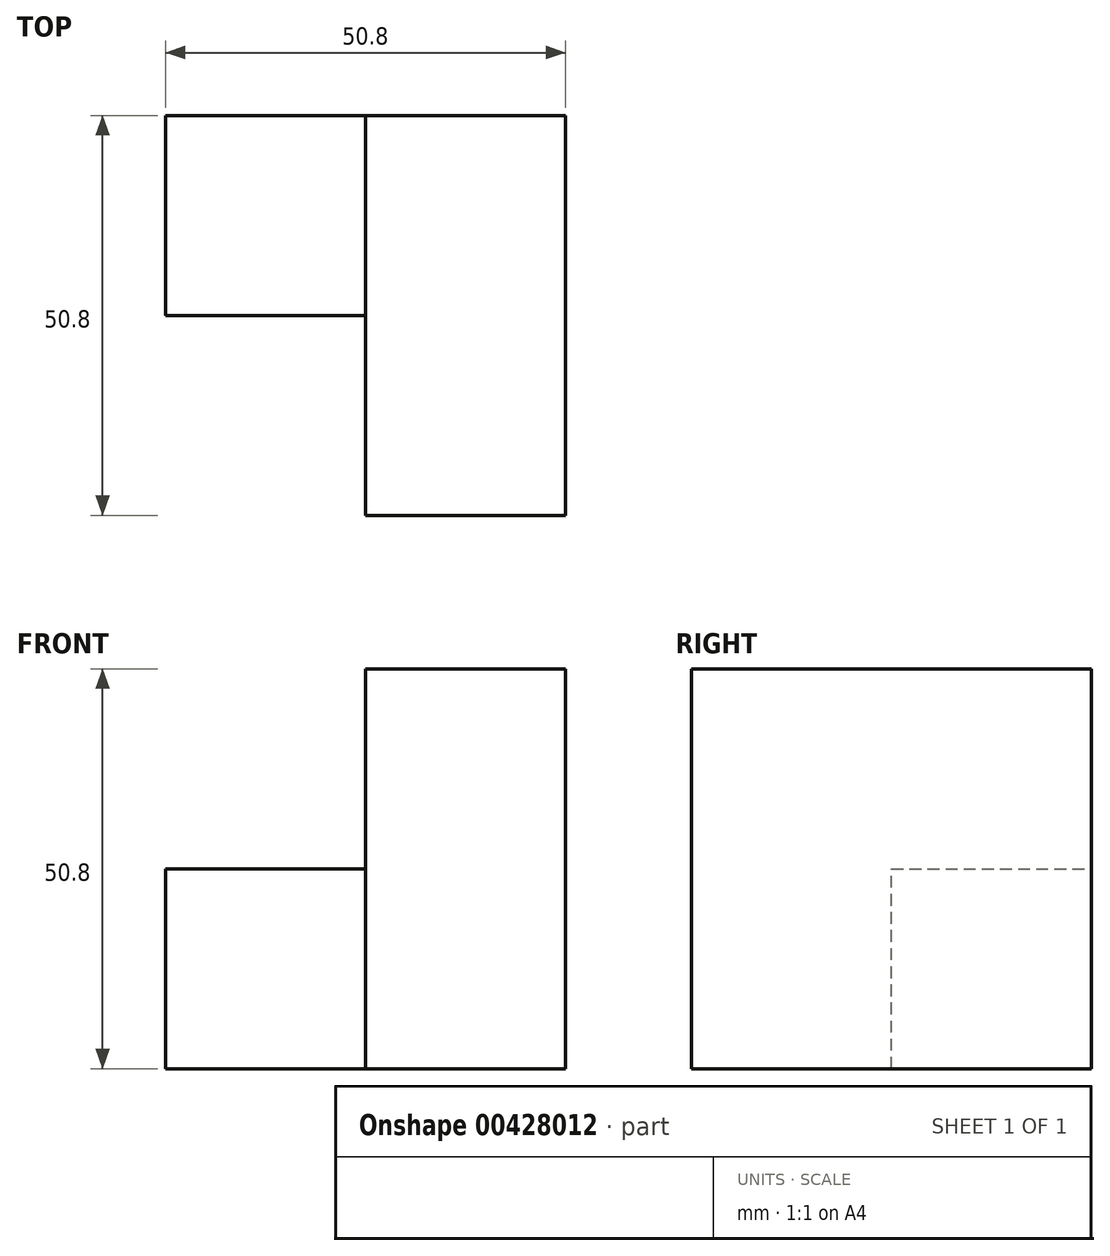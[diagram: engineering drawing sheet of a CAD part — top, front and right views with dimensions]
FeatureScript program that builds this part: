
annotation { "Feature Type Name" : "Feature", "Feature Type Description" : "" }
export const myFeature = defineFeature(function(context is Context, id is Id, definition is map)
    precondition{}
    {
        {
            var Q0;
            Q0=qCreatedBy(makeId("Front.planeOp"),FACE);
            var sketch = newSketch(context, id + "F0", { "sketchPlane" : qUnion([Q0])});
            skLineSegment(sketch, "E0.bottom", {"start": v(0, 0) * mm, "end": v(-25.4, 0) * mm});
            skLineSegment(sketch, "E0.top", {"start": v(0, 50.8) * mm, "end": v(-25.4, 50.8) * mm});
            skLineSegment(sketch, "E0.left", {"start": v(0, 0) * mm, "end": v(0, 50.8) * mm});
            skLineSegment(sketch, "E0.right", {"start": v(-25.4, 0) * mm, "end": v(-25.4, 50.8) * mm});
            skSolve(sketch);
        }
        {
            var Q0;
            Q0 = qSketchRegion(id + "F0", true);
            extrude(context, id + "F1", {"entities" : qUnion([Q0]), "depth" : 50.8 * mm});
        }
        {
            var Q0;
            Q0=qCreatedBy(makeId("Front.planeOp"),FACE);
            var sketch = newSketch(context, id + "F2", { "sketchPlane" : qUnion([Q0])});
            skLineSegment(sketch, "E1", {"start": v(0, 0) * mm, "end": v(-50.8, 0) * mm});
            skLineSegment(sketch, "E2", {"start": v(-50.8, 0) * mm, "end": v(-50.8, 25.4) * mm});
            skLineSegment(sketch, "E3", {"start": v(-50.8, 25.4) * mm, "end": v(0, 25.4) * mm});
            skPoint(sketch, "E4.end.orphan", {"position": v(2.7, 0) * mm});
            skLineSegment(sketch, "E5", {"start": v(0, 25.4) * mm, "end": v(0, 0) * mm});
            skSolve(sketch);
        }
        {
            var Q0;
            Q0 = qSketchRegion(id + "F2", true);
            extrude(context, id + "F3", {"entities" : qUnion([Q0]), "operationType" : NewBodyOperationType.ADD, "depth" : 25.4 * mm});
        }
    });
